# Revit family: IS_Ceraflex_BC135_BIM_IT
name_source: partatom
category: Plumbing Fixtures
revit_build: Autodesk Revit 2017 (Build: 20160225_1515(x64)
units: mm (PartAtom-declared; Revit-internal decimal feet)

## family parameters
Always vertical = No
Cut with Voids When Loaded = No
OmniClass Number = 23.45.55.17
OmniClass Title = Mixing Faucets
Part Type = Normal
Room Calculation Point = No
Round Connector Dimension = Use Diameter
Shared = No
Work Plane-Based = No

## types (1)
- BC135AA - CERAFLEX SNK MXR RMTD HIGH SPT/SLDR
    Accessori = www.idealstandard.it
    AltezzaNominale = 241 mm
    Autore = Ideal Standard
    BIMobject category = Taps & Mixers
    BIMobject category code = kitchen-taps
    BIMobject main category = Kitchen
    BIMobject main category code = kitchen
    BOSUseNativeGeometries = 1
    Brand = Ideal Standard
    Brand url = http://www.idealstandard.it
    Caratteristiche = Ceraflex - Miscelatore monocomando da appoggio su lavello.
    CodiceABarre = 3800861062134
    CodiceDiPrestazione = EN
    Colore = Cromo
    Connessione = piombatura
    CostoDiSostituzione = 0 $
    Date of publishing = 2019_01_04
    Description = Ceraflex - Miscelatore monocomando da appoggio su lavello.
    DescrizioneClassifcazioneUni2015 = Sink taps
    Desrizione = Ceraflex - Miscelatore monocomando da appoggio su lavello.
    Dimensione = 1850 x 95 x 720 mm
    DimensioneScarico = 0
    EAN code = https://3800861062134
    Edition number = 1
    Finitura = cromo
    Forma = Cilindrico
    Garanzia = Garanzia Ideal Standard
    Grado = n/s
    IFC Classification = IfcSanitaryTerminal
    IfcEsportaCome = Tap-Mixer
    InformazioniDiProdotto = http://www.idealstandard.it
    Installation instructions = http://www.idealstandard.it
    Installazione = http://www.idealstandard.it
    InstruzioniInstallazione = http://www.idealstandard.it
    LarghezzaNominale = 51 mm
    LunghezzaNominale = 260 mm
    Maniglia = No
    Manufacturer name = Ideal Standard
    Material main = Brass
    Materiale = Brass
    Model = BC135AA
    ModelloDiRiferimento = Ceraflex - Miscelatore monocomando da appoggio su lavello.
    NBS Reference Code = 45-35-70-345
    NBS Reference Description = Water supply fittings for sink
    Nome = Water supply fittings for sink_Ceraflex_BC135AA_IdealStandard
    NomeOggettoBim = ISI_IdealStandard_Water supply fittings for sink_Ceraflex_BC135AA
    Nominal depth = 0
    Nominal height = 0
    NominalHeight = 241 mm
    NominalLength = 260 mm
    NominalWidth = 51 mm
    NumeroDiModello = BC132AA
    OmniClass Code = 23-31 11 00
    OmniClass Description = Faucets
    PartiDiRicambio = http://www.idealstandard.it
    PesoNetto = 27.9
    PiattoDoccia = No
    Product Guid = 7314f8fb-5252-4c81-a92d-a3dca65d3213
    Product SKU = BC135
    Product certification = http://www.idealstandard.it
    Product data url = https://bimobject.com
    Product family = Sanitary
    Product group = Bath thermostatic water supply sets
    Product name = CERAFLEX SNK MXR RMTD HIGH SPT/SLDR
    Product url = http://www.idealstandard.it
    ProfonditaNominale = 0 mm  [stored 0 ft]
    QR code = http://bimobject.com
    Revisione = 1
    RiferimentoClassificazioneUni2015 = Pr_40_20_87_84
    SeatMaterial = 0 mm  [stored 0 ft]
    Size = 1850 x 95 x 720 mm
    SpessoreDelMateriale = 0
    SpilloverLivello = 0
    Technical description = http://www.idealstandard.it
    Telefono = 800 652 290
    TipoDiDato = Fisso
    TipoEspotazioneIfc = IfcSanitaryTerminalType
    URL = http://www.idealstandard.it
    Uniclass 2.0 Code = PR-35-79-79
    Uniclass 2.0 Description = Sink Water Supply Fittings
    Uniclass 2015 Code = Pr_40_20_87_84
    Uniclass 2015 Name = Sink taps
    UnitàDurata = anni
    UnitàDurataGaranzia = anni
    UnitàLineare = millimetri
    UnitàMonetaria = €
    UnitàSuperficie = €
    UnitàVolume = millimetri
    Versione = 1
    VersioneClassificazioneUni2015 = 1
    Weight Net (Kg) = 0
    Youtube clip = https://www.youtube.com

note: [stored X ft] marks values corroborated as IEEE doubles in the binary element streams (Revit-internal decimal feet)

## geometry (parser evidence)
native form markers: Sweep x2
no freeform markers — native parametric forms only
